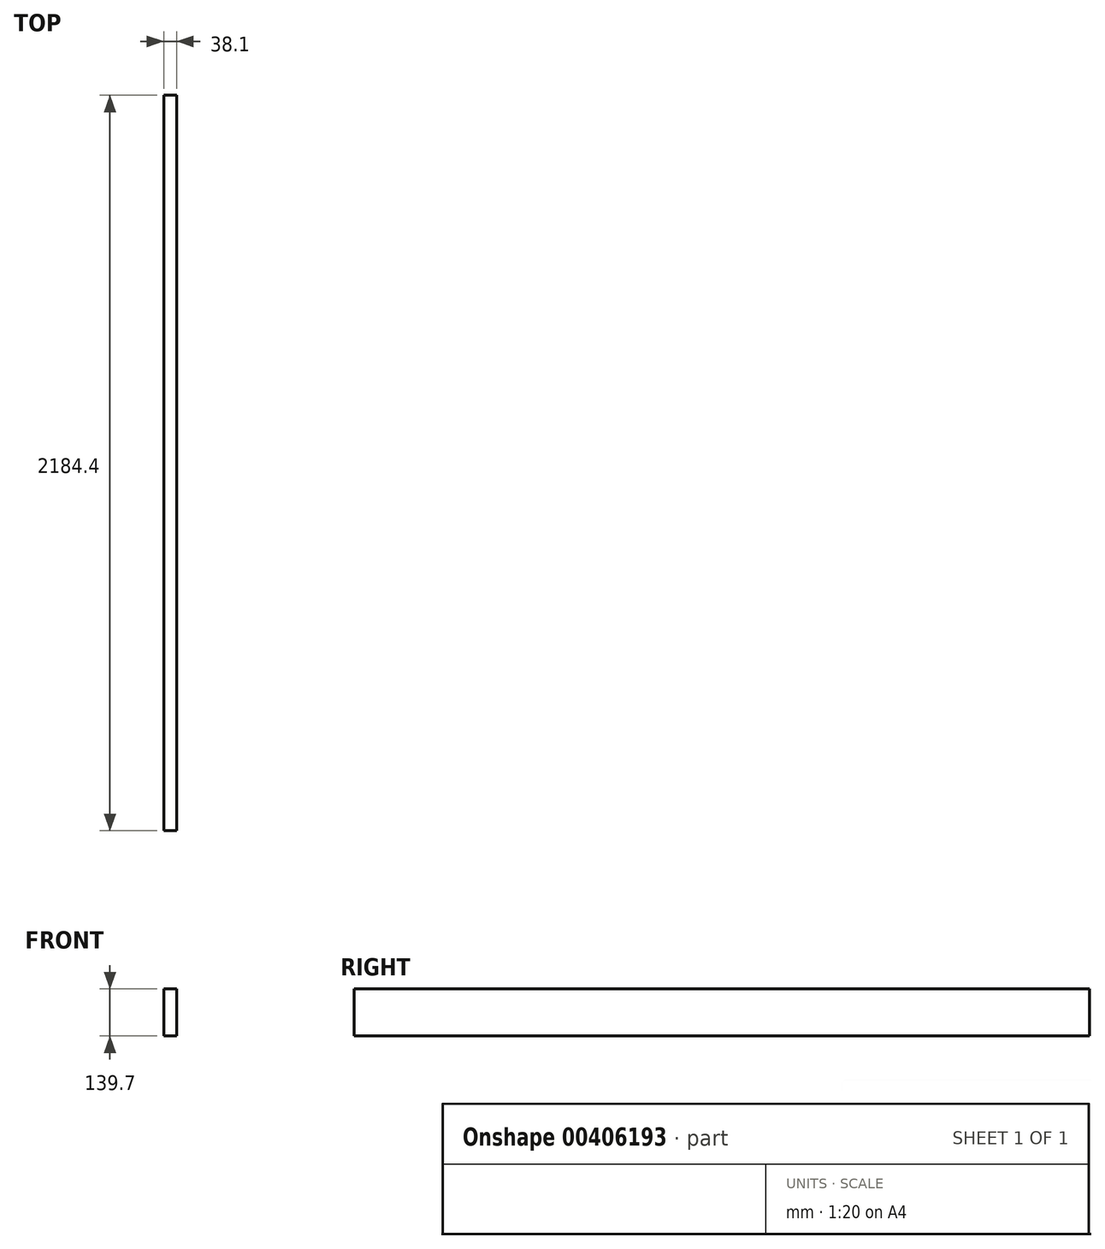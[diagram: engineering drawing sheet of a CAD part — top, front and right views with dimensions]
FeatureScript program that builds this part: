
annotation { "Feature Type Name" : "Feature", "Feature Type Description" : "" }
export const myFeature = defineFeature(function(context is Context, id is Id, definition is map)
    precondition{}
    {
        {
            var Q0;
            Q0=qCreatedBy(makeId("Front.planeOp"),FACE);
            var sketch = newSketch(context, id + "F0", { "sketchPlane" : qUnion([Q0])});
            skLineSegment(sketch, "E0.bottom", {"start": v(-19.05, -69.85) * mm, "end": v(19.05, -69.85) * mm});
            skLineSegment(sketch, "E0.top", {"start": v(-19.05, 69.85) * mm, "end": v(19.05, 69.85) * mm});
            skLineSegment(sketch, "E0.left", {"start": v(-19.05, -69.85) * mm, "end": v(-19.05, 69.85) * mm});
            skLineSegment(sketch, "E0.right", {"start": v(19.05, -69.85) * mm, "end": v(19.05, 69.85) * mm});
            skPoint(sketch, "E0.middle", {"position": v(0, 0) * mm});
            skSolve(sketch);
        }
        {
            var Q0;
            Q0=makeQuery(id+"F0.imprint","IMPRINT",FACE,{"disambiguationData":[TD([[makeQuery(id+"F0.imprint","IMPRINT",EDGE,{"derivedFrom":sQuery(id+"F0.wireOp",EDGE,"E0.bottom")}),1.0]])]});
            extrude(context, id + "F1", {"entities" : qUnion([Q0]), "oppositeDirection" : true, "depth" : 2184.4 * mm});
        }
    });
